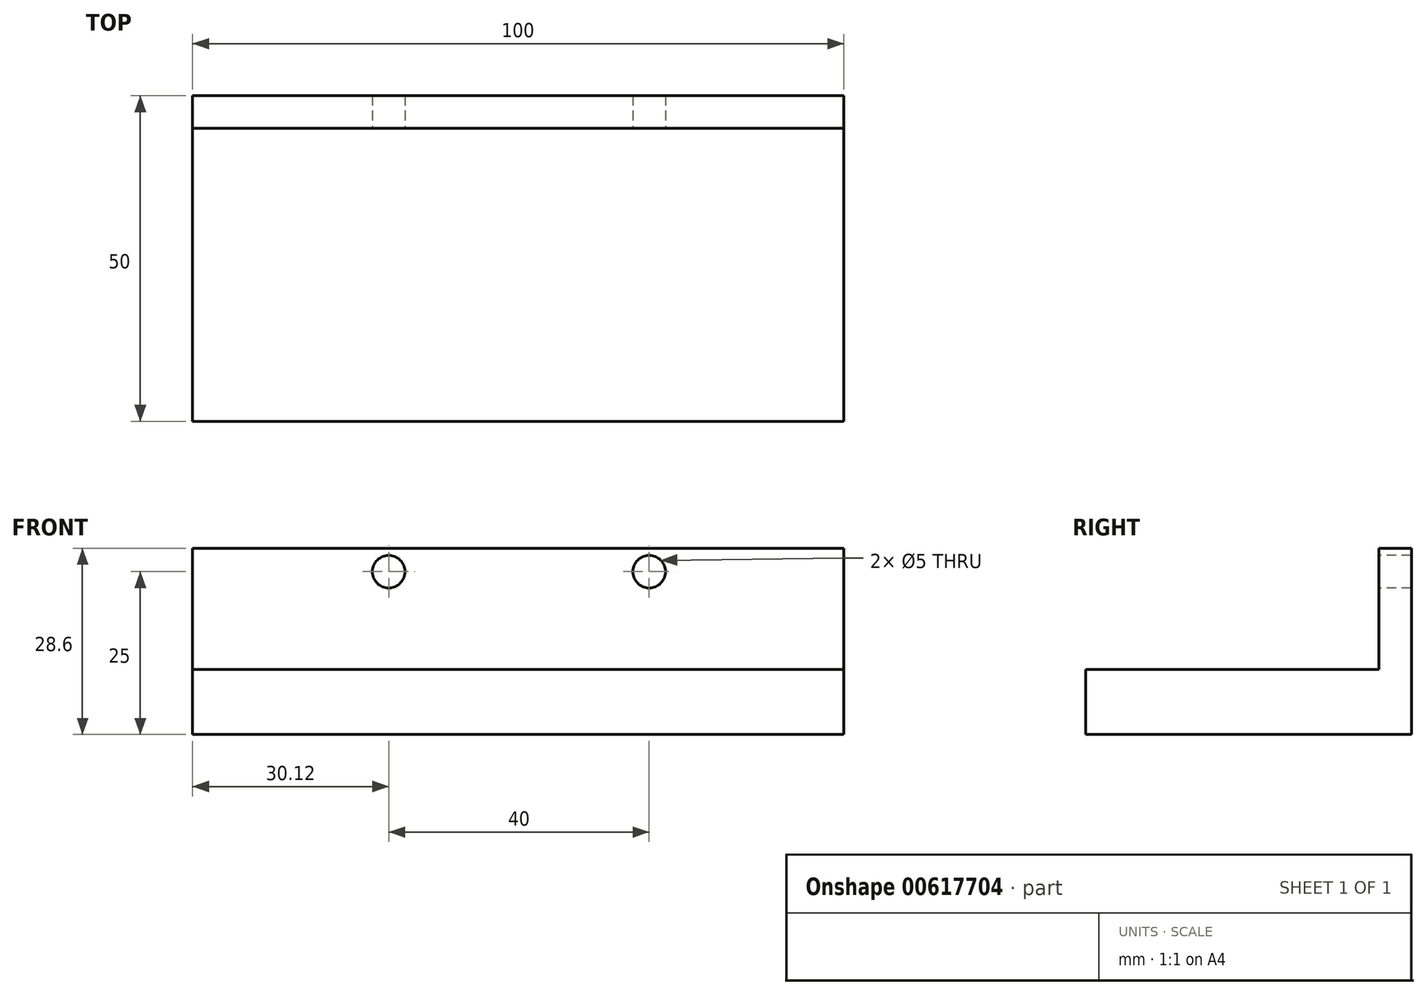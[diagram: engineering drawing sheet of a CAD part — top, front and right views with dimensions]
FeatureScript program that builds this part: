
annotation { "Feature Type Name" : "Feature", "Feature Type Description" : "" }
export const myFeature = defineFeature(function(context is Context, id is Id, definition is map)
    precondition{}
    {
        {
            var Q0;
            Q0=qCreatedBy(makeId("Top.planeOp"),FACE);
            var sketch = newSketch(context, id + "F0", { "sketchPlane" : qUnion([Q0])});
            skLineSegment(sketch, "E0.bottom", {"start": v(-50.12, 0) * mm, "end": v(49.88, 0) * mm});
            skLineSegment(sketch, "E0.top", {"start": v(-50.12, -50) * mm, "end": v(49.88, -50) * mm});
            skLineSegment(sketch, "E0.left", {"start": v(-50.12, 0) * mm, "end": v(-50.12, -50) * mm});
            skLineSegment(sketch, "E0.right", {"start": v(49.88, 0) * mm, "end": v(49.88, -50) * mm});
            skSolve(sketch);
        }
        {
            var Q0;
            Q0 = qSketchRegion(id + "F0", true);
            extrude(context, id + "F1", {"entities" : qUnion([Q0]), "depth" : 10 * mm, "offsetDistance" : 25 * mm});
        }
        {
            var Q0;
            Q0=makeQuery(id+"F1.opExtrude","CAP_FACE",FACE,{"disambiguationData":[OSD([sQuery(id+"F0.wireOp",EDGE,"E0.bottom"),sQuery(id+"F0.wireOp",EDGE,"E0.top"),sQuery(id+"F0.wireOp",EDGE,"E0.left"),sQuery(id+"F0.wireOp",EDGE,"E0.right")])],"isStart":false});
            var sketch = newSketch(context, id + "F2", { "sketchPlane" : qUnion([Q0])});
            skLineSegment(sketch, "E1.bottom", {"start": v(-50.12, 0) * mm, "end": v(49.88, 0) * mm});
            skLineSegment(sketch, "E1.top", {"start": v(-50.12, -5) * mm, "end": v(49.88, -5) * mm});
            skLineSegment(sketch, "E1.left", {"start": v(-50.12, 0) * mm, "end": v(-50.12, -5) * mm});
            skLineSegment(sketch, "E1.right", {"start": v(49.88, 0) * mm, "end": v(49.88, -5) * mm});
            skSolve(sketch);
        }
        {
            var Q0;
            Q0 = qSketchRegion(id + "F2", true);
            extrude(context, id + "F3", {"entities" : qUnion([Q0]), "operationType" : NewBodyOperationType.ADD, "depth" : 18.6 * mm, "offsetDistance" : 25 * mm});
        }
        {
            var Q0;
            Q0=makeQuery(id+"F3.opExtrude","SWEPT_FACE",FACE,{"disambiguationData":[OSD([sQuery(id+"F2.wireOp",EDGE,"E1.top")])]});
            var sketch = newSketch(context, id + "F4", { "sketchPlane" : qUnion([Q0])});
            skCircle(sketch, "E2", {"center": v(20, 25) * mm, "radius": 2.5 * mm});
            skCircle(sketch, "E3", {"center": v(-20, 25) * mm, "radius": 2.5 * mm});
            skSolve(sketch);
        }
        {
            var Q0;
            Q0 = qSketchRegion(id + "F4", true);
            extrude(context, id + "F5", {"entities" : qUnion([Q0]), "operationType" : NewBodyOperationType.REMOVE, "endBound" : BoundingType.THROUGH_ALL, "oppositeDirection" : true, "depth" : 25 * mm, "offsetDistance" : 25 * mm});
        }
    });
